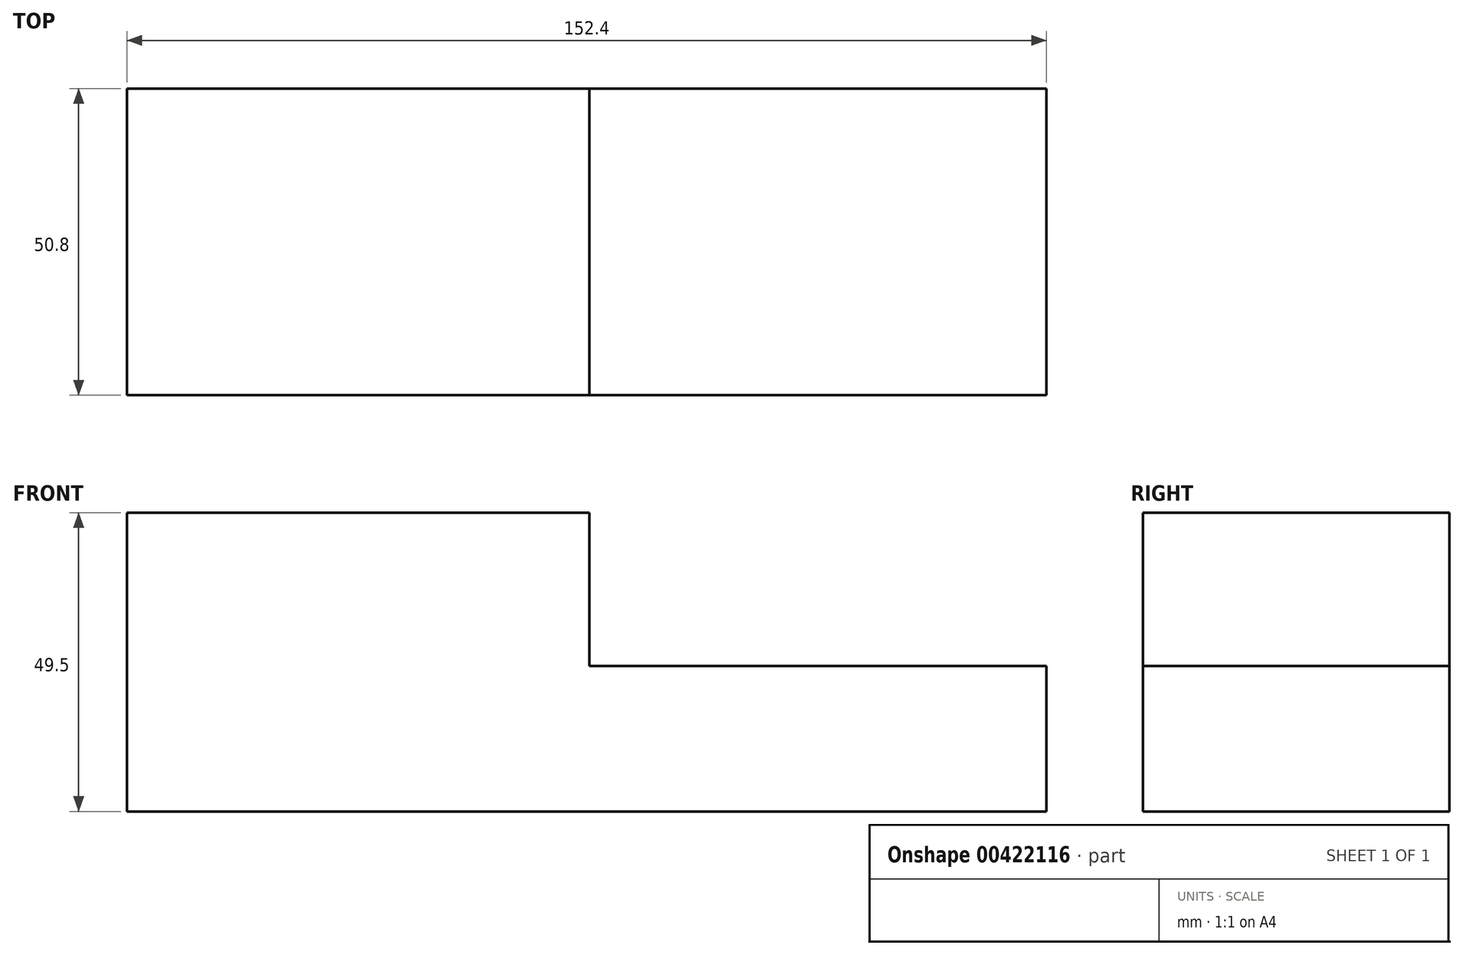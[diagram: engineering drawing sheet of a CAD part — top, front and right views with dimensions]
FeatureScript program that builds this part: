
annotation { "Feature Type Name" : "Feature", "Feature Type Description" : "" }
export const myFeature = defineFeature(function(context is Context, id is Id, definition is map)
    precondition{}
    {
        {
            var Q0;
            Q0=qCreatedBy(makeId("Front.planeOp"),FACE);
            var sketch = newSketch(context, id + "F0", { "sketchPlane" : qUnion([Q0])});
            skLineSegment(sketch, "E0", {"start": v(0, 0) * mm, "end": v(152.4, 0) * mm});
            skLineSegment(sketch, "E1", {"start": v(152.4, 0) * mm, "end": v(152.4, 24.1) * mm});
            skLineSegment(sketch, "E2", {"start": v(152.4, 24.1) * mm, "end": v(76.66, 24.1) * mm});
            skLineSegment(sketch, "E3", {"start": v(76.66, 24.1) * mm, "end": v(76.66, 49.5) * mm});
            skLineSegment(sketch, "E4", {"start": v(76.66, 49.5) * mm, "end": v(0, 49.5) * mm});
            skLineSegment(sketch, "E5", {"start": v(0, 49.5) * mm, "end": v(0, 0) * mm});
            skSolve(sketch);
        }
        {
            var Q0;
            Q0=makeQuery(id+"F0.imprint","IMPRINT",FACE,{"disambiguationData":[TD([[makeQuery(id+"F0.imprint","IMPRINT",EDGE,{"derivedFrom":sQuery(id+"F0.wireOp",EDGE,"E0")}),1.0]])]});
            extrude(context, id + "F1", {"entities" : qUnion([Q0]), "depth" : 50.8 * mm});
        }
    });
